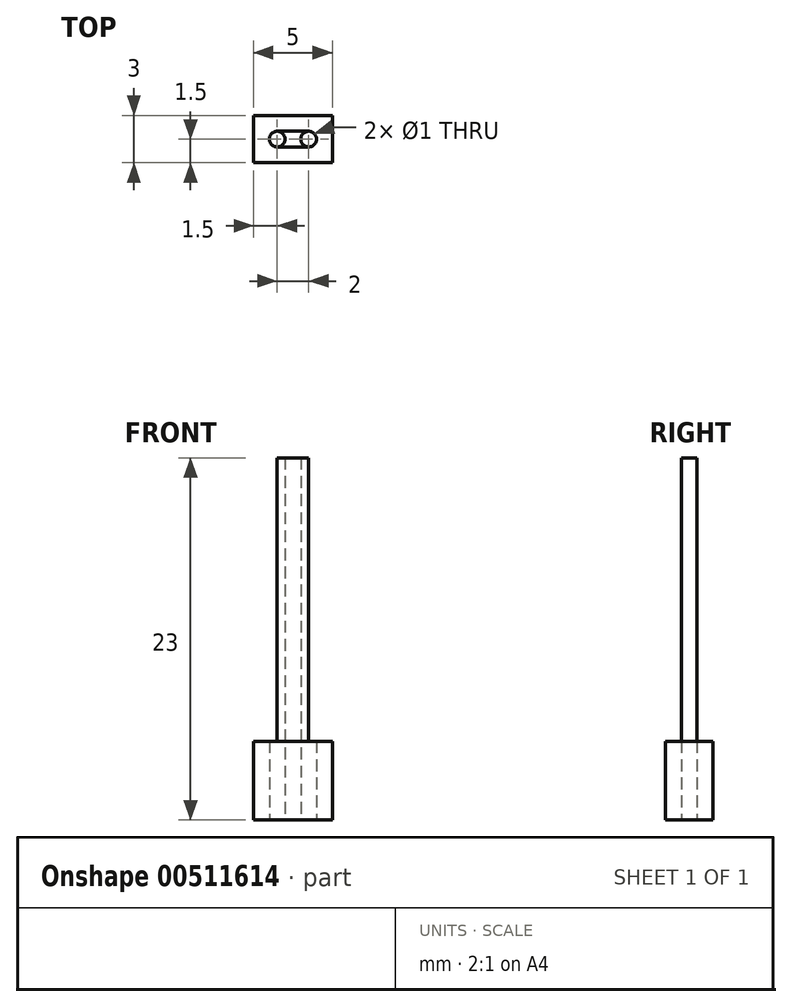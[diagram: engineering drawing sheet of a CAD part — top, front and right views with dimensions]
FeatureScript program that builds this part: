
annotation { "Feature Type Name" : "Feature", "Feature Type Description" : "" }
export const myFeature = defineFeature(function(context is Context, id is Id, definition is map)
    precondition{}
    {
        {
            var Q0;
            Q0=qCreatedBy(makeId("Top.planeOp"),FACE);
            var sketch = newSketch(context, id + "F0", { "sketchPlane" : qUnion([Q0])});
            skLineSegment(sketch, "E0.bottom", {"start": v(2.5, 1.5) * mm, "end": v(-2.5, 1.5) * mm});
            skLineSegment(sketch, "E0.top", {"start": v(2.5, -1.5) * mm, "end": v(-2.5, -1.5) * mm});
            skLineSegment(sketch, "E0.left", {"start": v(2.5, 1.5) * mm, "end": v(2.5, -1.5) * mm});
            skLineSegment(sketch, "E0.right", {"start": v(-2.5, 1.5) * mm, "end": v(-2.5, -1.5) * mm});
            skPoint(sketch, "E0.middle", {"position": v(0, 0) * mm});
            skLineSegment(sketch, "E1", {"start": v(0, 0) * mm, "end": v(1, 0) * mm});
            skCircle(sketch, "E2", {"center": v(1, 0) * mm, "radius": 0.5 * mm});
            skCircle(sketch, "E3.MirrorC", {"center": v(-1, 0) * mm, "radius": 0.5 * mm});
            skLineSegment(sketch, "E4", {"start": v(1, 0) * mm, "end": v(1, 0.5) * mm});
            skLineSegment(sketch, "E5", {"start": v(-1, 0) * mm, "end": v(-1, 0.5) * mm});
            skLineSegment(sketch, "E6", {"start": v(-1, 0.5) * mm, "end": v(1, 0.5) * mm});
            skLineSegment(sketch, "E7", {"start": v(-1, 0) * mm, "end": v(-1, -0.5) * mm});
            skLineSegment(sketch, "E8", {"start": v(-1, -0.5) * mm, "end": v(1, -0.5) * mm});
            skLineSegment(sketch, "E9", {"start": v(1, -0.5) * mm, "end": v(1, 0) * mm});
            skSolve(sketch);
        }
        {
            var Q0;
            Q0=qSketchRegion(id+"F0",true);
            extrude(context, id + "F1", {"entities" : qUnion([Q0]), "depth" : 5 * mm, "offsetDistance" : 25 * mm});
        }
        {
            var Q0;
            {var subQ0=sQuery(id+"F0.wireOp",EDGE,"E6");Q0=makeQuery(id+"F0.imprint","IMPRINT",FACE,{"disambiguationData":[TD([[makeQuery(id+"F0.imprint","IMPRINT",EDGE,{"derivedFrom":subQ0}),-1.0]])]});}
            extrude(context, id + "F2", {"entities" : qUnion([Q0]), "operationType" : NewBodyOperationType.ADD, "depth" : 23 * mm, "offsetDistance" : 25 * mm});
        }
    });
